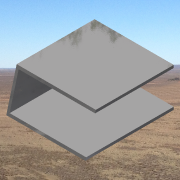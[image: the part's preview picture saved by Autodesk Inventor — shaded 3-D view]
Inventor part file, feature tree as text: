
AUTODESK INVENTOR PART (.ipt)
format: ipt  version: 2013 SP2 (Build 170200200, 200)  size: 132,608 bytes
history: native  units: in
note: dims shown in document units (in); Inventor stores cm internally (conversion verified against a paired STEP export)
features: extrude x3, sketch x3, plane x1
ambient origin geometry x8: Origin, YZ Plane, XZ Plane, XY Plane, X Axis, Y Axis, Z Axis, Center Point
bodies: Solid1 (feature_tree)
feature tree (7):
  extrude  "Extrusion1"  Depth=1.5in
  plane  "Work Plane2"
  extrude  "Extrusion3"  Depth=4.0in TaperAngle=0.0deg
  extrude  "Extrusion4"  Depth=0.5in TaperAngle=0.0deg
  sketch  "Sketch1"  dims[d0=3.5in d1=1.5in]
  sketch  "Sketch3"  dims[d2=0.12in d3=4.0in d4=0.0in]
  sketch  "Sketch4"  dims[d10=-0.5154in d11=0.5in d12=0.0in d13=0.2in d14=0.0in]
